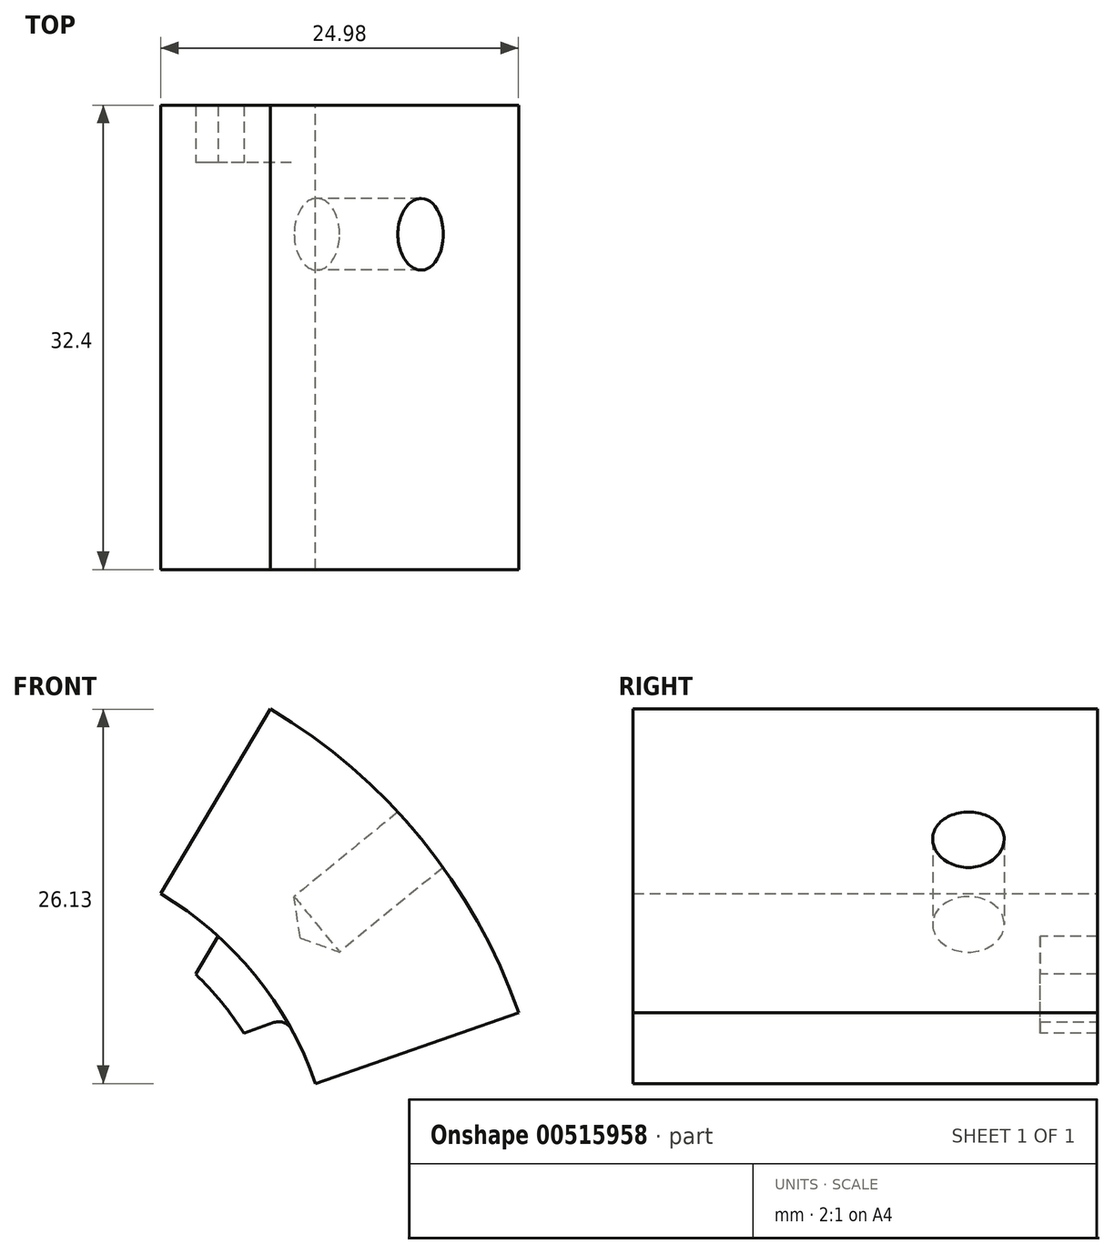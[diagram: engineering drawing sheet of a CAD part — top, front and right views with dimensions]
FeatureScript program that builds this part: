
annotation { "Feature Type Name" : "Feature", "Feature Type Description" : "" }
export const myFeature = defineFeature(function(context is Context, id is Id, definition is map)
    precondition{}
    {
        {
            var Q0;
            Q0=qCreatedBy(makeId("Front.planeOp"),FACE);
            var sketch = newSketch(context, id + "F0", { "sketchPlane" : qUnion([Q0])});
            skArc(sketch, "E0", {"start": v(37.76, 13.18) * mm, "mid": v(30.98, 25.3) * mm, "end": v(20.45, 34.37) * mm});
            skArc(sketch, "E1", {"start": v(23.6, 8.24) * mm, "mid": v(19.36, 15.82) * mm, "end": v(12.78, 21.48) * mm});
            skLineSegment(sketch, "E2", {"start": v(12.78, 21.48) * mm, "end": v(20.45, 34.37) * mm});
            skLineSegment(sketch, "E3", {"start": v(23.6, 8.24) * mm, "end": v(37.76, 13.18) * mm});
            skSolve(sketch);
        }
        {
            var Q0;
            Q0=qCreatedBy(makeId("Front.planeOp"),FACE);
            var sketch = newSketch(context, id + "F1", { "sketchPlane" : qUnion([Q0])});
            skArc(sketch, "E4", {"start": v(18.6, 11.76) * mm, "mid": v(17.04, 13.92) * mm, "end": v(15.23, 15.87) * mm});
            skLineSegment(sketch, "E5", {"start": v(20.5, 34.46) * mm, "end": v(12.78, 21.48) * mm});
            skLineSegment(sketch, "E6", {"start": v(37.76, 13.18) * mm, "end": v(23.6, 8.24) * mm});
            skArc(sketch, "E7", {"start": v(37.76, 13.18) * mm, "mid": v(30.98, 25.3) * mm, "end": v(20.45, 34.37) * mm});
            skArc(sketch, "E8", {"start": v(23.6, 8.24) * mm, "mid": v(22.66, 10.56) * mm, "end": v(21.5, 12.77) * mm});
            skLineSegment(sketch, "E9", {"start": v(21.5, 12.77) * mm, "end": v(18.6, 11.76) * mm});
            skLineSegment(sketch, "E10", {"start": v(16.8, 18.51) * mm, "end": v(15.23, 15.87) * mm});
            skArc(sketch, "E11.trimOffspring", {"start": v(16.8, 18.51) * mm, "mid": v(14.87, 20.1) * mm, "end": v(12.78, 21.48) * mm});
            skSolve(sketch);
        }
        {
            var Q0;
            Q0=makeQuery(id+"F0.imprint","IMPRINT",FACE,{"disambiguationData":[TD([[makeQuery(id+"F0.imprint","IMPRINT",EDGE,{"derivedFrom":sQuery(id+"F0.wireOp",EDGE,"E0")}),1.0]])]});
            extrude(context, id + "F2", {"entities" : qUnion([Q0]), "depth" : 28.4 * mm, "offsetDistance" : 25 * mm});
        }
        {
            var Q0;
            Q0=qSketchRegion(id+"F1",true);
            var Q1;
            Q1=qSketchRegion(id+"F0",true);
            extrude(context, id + "F3", {"entities" : qUnion([Q0, Q1]), "operationType" : NewBodyOperationType.ADD, "oppositeDirection" : true, "depth" : 4 * mm, "offsetDistance" : 25 * mm});
        }
        {
            var Q0;
            Q0=makeQuery(id+"F2.opExtrude","CAP_VERTEX",VERTEX,{"disambiguationData":[OSD([sQuery(id+"F0.wireOp",EDGE,"E0"),sQuery(id+"F0.wireOp",EDGE,"E3")])],"isStart":false});
            var Q1;
            Q1=makeQuery(id+"F2.opExtrude","CAP_VERTEX",VERTEX,{"disambiguationData":[OSD([sQuery(id+"F0.wireOp",EDGE,"E0"),sQuery(id+"F0.wireOp",EDGE,"E2")])],"isStart":false});
            var Q2;
            Q2=sQuery(id+"F0.wireOp",VERTEX,"E2.end");
            cPlane(context, id + "F4", {"entities" : qUnion([Q0, Q1, Q2]), "cplaneType" : CPlaneType.THREE_POINT, "offset" : 0 * mm, "width" : 150 * mm, "height" : 150 * mm});
        }
        {
            var Q0;
            Q0=qCreatedBy(id+"F4.planeOp",FACE);
            var sketch = newSketch(context, id + "F5", { "sketchPlane" : qUnion([Q0])});
            skCircle(sketch, "E12", {"center": v(-5, 0) * mm, "radius": 2.5 * mm});
            skSolve(sketch);
        }
        {
            var Q0;
            Q0=sQuery(id+"F5.wireOp",VERTEX,"E12.center");
            var Q1;
            Q1=makeQuery(id+"F2.opExtrude","SWEPT_BODY",BODY,{"disambiguationData":[OSD([sQuery(id+"F0.wireOp",EDGE,"E0"),sQuery(id+"F0.wireOp",EDGE,"E1"),sQuery(id+"F0.wireOp",EDGE,"E2"),sQuery(id+"F0.wireOp",EDGE,"E3")])]});
            hole(context, id + "F6", {"style" : HoleStyle.SIMPLE, "endStyle" : HoleEndStyle.BLIND, "oppositeDirection" : true, "holeDiameter" : 5 * mm, "holeDepth" : 5 * mm, "isTappedThrough" : true, "tappedDepth" : 12 * mm, "tapClearance" : 3, "startFromSketch" : true, "locations" : qUnion([Q0]), "scope" : qUnion([Q1])});
        }
        {
            var Q0;
            Q0=sQuery(id+"F5.wireOp",VERTEX,"E12.center");
            var Q1;
            Q1=makeQuery(id+"F2.opExtrude","SWEPT_BODY",BODY,{"disambiguationData":[OSD([sQuery(id+"F0.wireOp",EDGE,"E0"),sQuery(id+"F0.wireOp",EDGE,"E1"),sQuery(id+"F0.wireOp",EDGE,"E2"),sQuery(id+"F0.wireOp",EDGE,"E3")])]});
            hole(context, id + "F7", {"style" : HoleStyle.SIMPLE, "endStyle" : HoleEndStyle.BLIND, "holeDiameter" : 5 * mm, "holeDepth" : 7 * mm, "isTappedThrough" : true, "tappedDepth" : 12 * mm, "tapClearance" : 3, "startFromSketch" : true, "locations" : qUnion([Q0]), "scope" : qUnion([Q1])});
        }
        {
            var Q0;
            Q0=makeQuery(id+"F3.opExtrude","SWEPT_EDGE",EDGE,{"disambiguationData":[OSD([sQuery(id+"F1.wireOp",EDGE,"E8"),sQuery(id+"F1.wireOp",EDGE,"E9")])]});
            var Q1;
            Q1=makeQuery(id+"F3.opExtrude","SWEPT_EDGE",EDGE,{"disambiguationData":[OSD([sQuery(id+"F1.wireOp",EDGE,"E10"),sQuery(id+"F1.wireOp",EDGE,"E11.trimOffspring")])]});
            fillet(context, id + "F8", {"entities" : qUnion([Q0, Q1]), "radius" : 1 * mm, "tangentPropagation" : true, "allowEdgeOverflow" : false});
        }
    });
